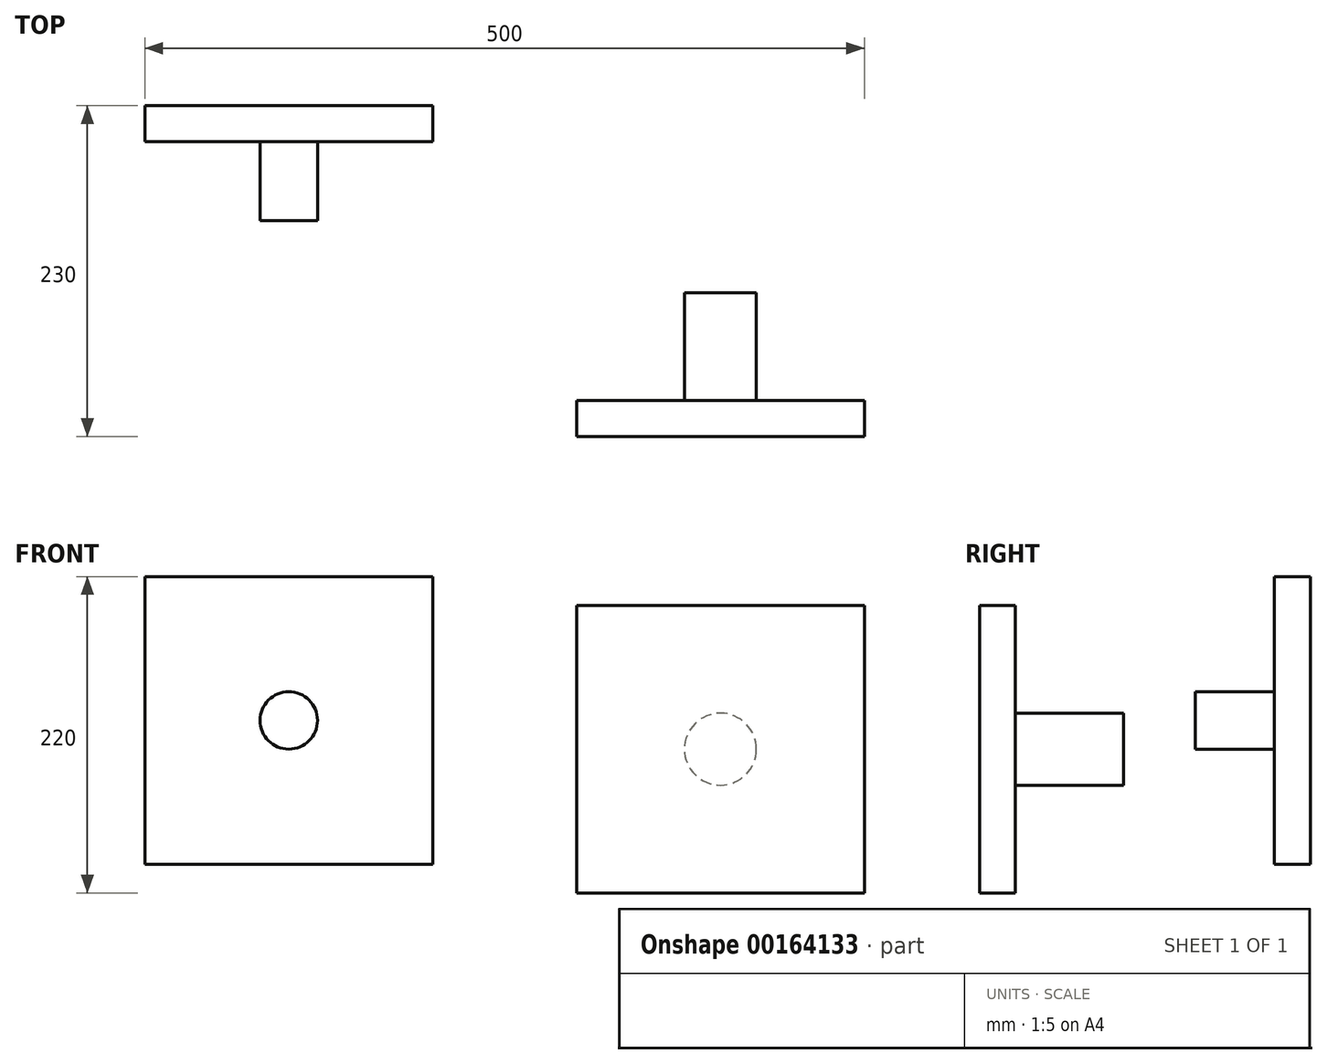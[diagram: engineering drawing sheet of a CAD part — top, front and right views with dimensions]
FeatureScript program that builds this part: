
annotation { "Feature Type Name" : "Feature", "Feature Type Description" : "" }
export const myFeature = defineFeature(function(context is Context, id is Id, definition is map)
    precondition{}
    {
        {
            var Q0;
            Q0=qCreatedBy(makeId("Front.planeOp"),FACE);
            var sketch = newSketch(context, id + "F0", { "sketchPlane" : qUnion([Q0])});
            skLineSegment(sketch, "E0.bottom", {"start": v(100, -100) * mm, "end": v(-100, -100) * mm});
            skLineSegment(sketch, "E0.top", {"start": v(100, 100) * mm, "end": v(-100, 100) * mm});
            skLineSegment(sketch, "E0.left", {"start": v(100, -100) * mm, "end": v(100, 100) * mm});
            skLineSegment(sketch, "E0.right", {"start": v(-100, -100) * mm, "end": v(-100, 100) * mm});
            skPoint(sketch, "E0.middle", {"position": v(0, 0) * mm});
            skCircle(sketch, "E1", {"center": v(0, 0) * mm, "radius": 25 * mm});
            skSolve(sketch);
        }
        {
            var Q0;
            Q0=makeQuery(id+"F0.imprint","IMPRINT",FACE,{"disambiguationData":[TD([[makeQuery(id+"F0.imprint","IMPRINT",EDGE,{"derivedFrom":sQuery(id+"F0.wireOp",EDGE,"E1")}),1.0]])]});
            extrude(context, id + "F1", {"entities" : qUnion([Q0]), "oppositeDirection" : true, "depth" : 100 * mm, "offsetDistance" : 25 * mm});
        }
        {
            var Q0;
            Q0=makeQuery(id+"F0.imprint","IMPRINT",FACE,{"disambiguationData":[TD([[makeQuery(id+"F0.imprint","IMPRINT",EDGE,{"derivedFrom":sQuery(id+"F0.wireOp",EDGE,"E0.bottom")}),-1.0]])]});
            extrude(context, id + "F2", {"entities" : qUnion([Q0]), "operationType" : NewBodyOperationType.ADD, "oppositeDirection" : true, "depth" : 25 * mm});
        }
        {
            var Q0;
            Q0=qCreatedBy(makeId("Front.planeOp"),FACE);
            cPlane(context, id + "F3", {"entities" : qUnion([Q0]), "cplaneType" : CPlaneType.OFFSET, "offset" : 230 * mm, "oppositeDirection" : true, "width" : 150 * mm, "height" : 150 * mm});
        }
        {
            var Q0;
            Q0=qCreatedBy(id+"F3.planeOp",FACE);
            var sketch = newSketch(context, id + "F4", { "sketchPlane" : qUnion([Q0])});
            skLineSegment(sketch, "E2.bottom", {"start": v(-200, -80) * mm, "end": v(-400, -80) * mm});
            skLineSegment(sketch, "E2.top", {"start": v(-200, 120) * mm, "end": v(-400, 120) * mm});
            skLineSegment(sketch, "E2.left", {"start": v(-200, -80) * mm, "end": v(-200, 120) * mm});
            skLineSegment(sketch, "E2.right", {"start": v(-400, -80) * mm, "end": v(-400, 120) * mm});
            skPoint(sketch, "E2.middle", {"position": v(-300, 20) * mm});
            skCircle(sketch, "E3", {"center": v(-300, 20) * mm, "radius": 20 * mm});
            skSolve(sketch);
        }
        {
            var Q0;
            Q0=makeQuery(id+"F4.imprint","IMPRINT",FACE,{"disambiguationData":[TD([[makeQuery(id+"F4.imprint","IMPRINT",EDGE,{"derivedFrom":sQuery(id+"F4.wireOp",EDGE,"E3")}),1.0]])]});
            extrude(context, id + "F5", {"entities" : qUnion([Q0]), "depth" : 80 * mm});
        }
        {
            var Q0;
            Q0=makeQuery(id+"F4.imprint","IMPRINT",FACE,{"disambiguationData":[TD([[makeQuery(id+"F4.imprint","IMPRINT",EDGE,{"derivedFrom":sQuery(id+"F4.wireOp",EDGE,"E2.bottom")}),-1.0]])]});
            extrude(context, id + "F6", {"entities" : qUnion([Q0]), "operationType" : NewBodyOperationType.ADD, "depth" : 25 * mm});
        }
    });
